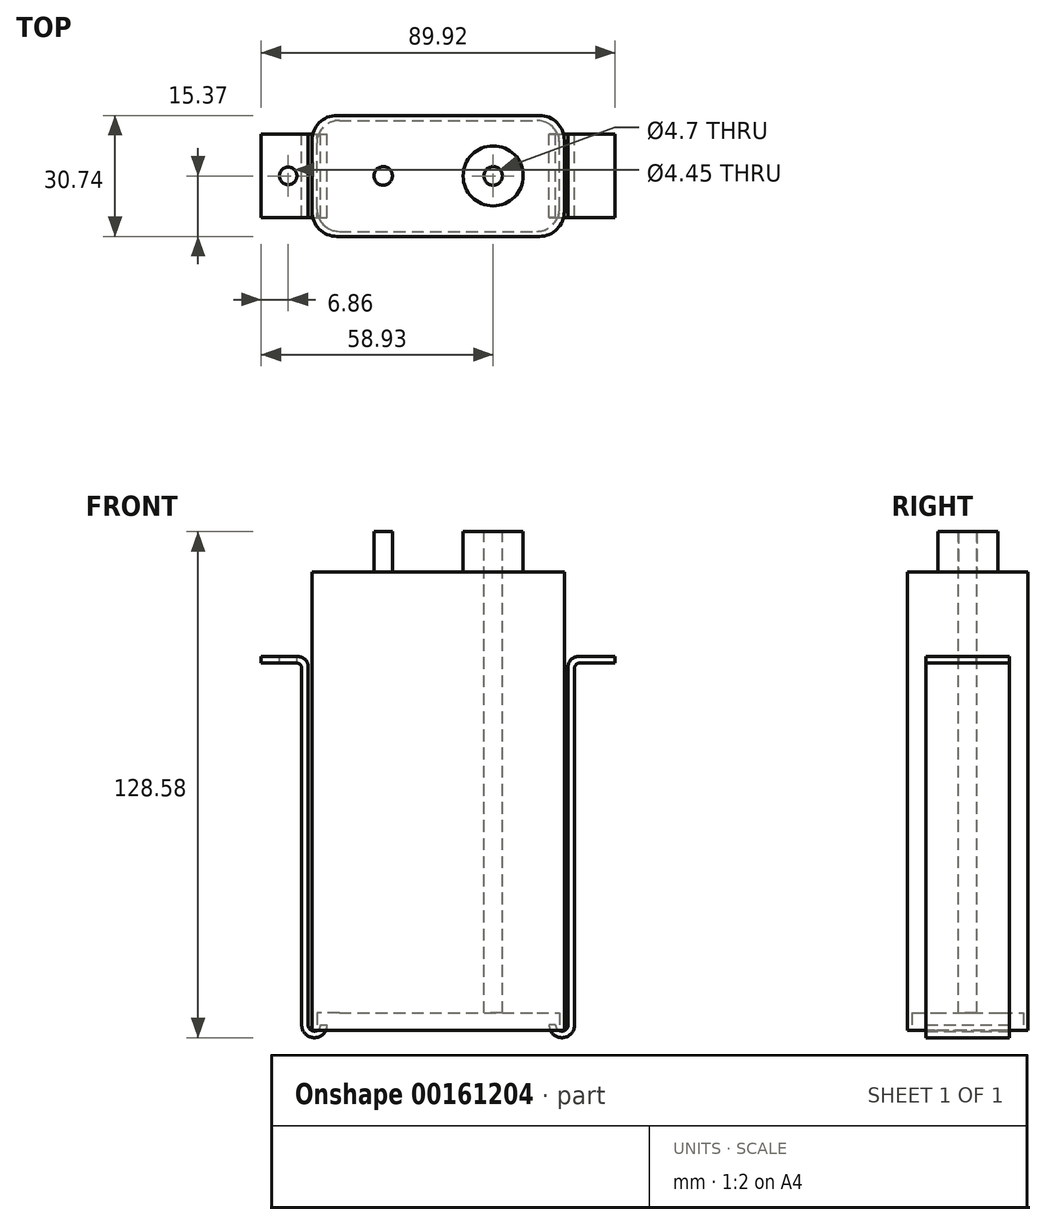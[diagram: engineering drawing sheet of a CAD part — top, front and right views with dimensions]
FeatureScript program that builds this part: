
annotation { "Feature Type Name" : "Feature", "Feature Type Description" : "" }
export const myFeature = defineFeature(function(context is Context, id is Id, definition is map)
    precondition{}
    {
        {
            var Q0;
            Q0=qCreatedBy(makeId("Top.planeOp"),FACE);
            var sketch = newSketch(context, id + "F0", { "sketchPlane" : qUnion([Q0])});
            skLineSegment(sketch, "E0.bottom", {"start": v(25.72, 15.37) * mm, "end": v(-25.72, 15.37) * mm});
            skLineSegment(sketch, "E0.top", {"start": v(25.72, -15.37) * mm, "end": v(-25.72, -15.37) * mm});
            skLineSegment(sketch, "E0.left", {"start": v(32.07, 9.02) * mm, "end": v(32.07, -9.02) * mm});
            skLineSegment(sketch, "E0.right", {"start": v(-32.07, 9.02) * mm, "end": v(-32.07, -9.02) * mm});
            skPoint(sketch, "E0.middle", {"position": v(0, 0) * mm});
            skPoint(sketch, "E1.visualSharp", {"position": v(-32.07, 15.37) * mm});
            skArc(sketch, "E1.filletArc", {"start": v(-25.72, 15.37) * mm, "mid": v(-30.2, 13.5) * mm, "end": v(-32.07, 9.02) * mm});
            skPoint(sketch, "E2.visualSharp", {"position": v(-32.07, -15.37) * mm});
            skArc(sketch, "E2.filletArc", {"start": v(-32.07, -9.02) * mm, "mid": v(-30.2, -13.5) * mm, "end": v(-25.72, -15.37) * mm});
            skPoint(sketch, "E3.visualSharp", {"position": v(32.07, -15.37) * mm});
            skArc(sketch, "E3.filletArc", {"start": v(25.72, -15.37) * mm, "mid": v(30.2, -13.5) * mm, "end": v(32.07, -9.02) * mm});
            skPoint(sketch, "E4.visualSharp", {"position": v(32.07, 15.37) * mm});
            skArc(sketch, "E4.filletArc", {"start": v(32.07, 9.02) * mm, "mid": v(30.2, 13.5) * mm, "end": v(25.72, 15.37) * mm});
            skCircle(sketch, "E5", {"center": v(-13.97, 0) * mm, "radius": 7.62 * mm});
            skCircle(sketch, "E6.MirrorC", {"center": v(13.97, 0) * mm, "radius": 7.62 * mm});
            skCircle(sketch, "E7", {"center": v(-13.97, 0) * mm, "radius": 2.35 * mm});
            skCircle(sketch, "E8.MirrorC", {"center": v(13.97, 0) * mm, "radius": 2.35 * mm});
            skSolve(sketch);
        }
        {
            var Q0;
            Q0=makeQuery(id+"F0.imprint","IMPRINT",FACE,{"disambiguationData":[TD([[makeQuery(id+"F0.imprint","IMPRINT",EDGE,{"derivedFrom":sQuery(id+"F0.wireOp",EDGE,"E0.bottom")}),1.0]])]});
            var Q1;
            Q1=makeQuery(id+"F0.imprint","IMPRINT",FACE,{"disambiguationData":[TD([[makeQuery(id+"F0.imprint","IMPRINT",EDGE,{"derivedFrom":sQuery(id+"F0.wireOp",EDGE,"E5")}),1.0]])]});
            var Q2;
            Q2=makeQuery(id+"F0.imprint","IMPRINT",FACE,{"disambiguationData":[TD([[makeQuery(id+"F0.imprint","IMPRINT",EDGE,{"derivedFrom":sQuery(id+"F0.wireOp",EDGE,"E7")}),1.0]])]});
            var Q3;
            Q3=makeQuery(id+"F0.imprint","IMPRINT",FACE,{"disambiguationData":[TD([[makeQuery(id+"F0.imprint","IMPRINT",EDGE,{"derivedFrom":sQuery(id+"F0.wireOp",EDGE,"E6.MirrorC")}),-1.0]])]});
            var Q4;
            Q4=makeQuery(id+"F0.imprint","IMPRINT",FACE,{"disambiguationData":[TD([[makeQuery(id+"F0.imprint","IMPRINT",EDGE,{"derivedFrom":sQuery(id+"F0.wireOp",EDGE,"E8.MirrorC")}),-1.0]])]});
            extrude(context, id + "F1", {"entities" : qUnion([Q0, Q1, Q2, Q3, Q4]), "oppositeDirection" : true, "depth" : 98.17 * mm});
        }
        {
            var Q0;
            Q0=makeQuery(id+"F0.imprint","IMPRINT",FACE,{"disambiguationData":[TD([[makeQuery(id+"F0.imprint","IMPRINT",EDGE,{"derivedFrom":sQuery(id+"F0.wireOp",EDGE,"E5")}),1.0]])]});
            var Q1;
            Q1=makeQuery(id+"F0.imprint","IMPRINT",FACE,{"disambiguationData":[TD([[makeQuery(id+"F0.imprint","IMPRINT",EDGE,{"derivedFrom":sQuery(id+"F0.wireOp",EDGE,"E7")}),1.0]])]});
            var Q2;
            Q2=makeQuery(id+"F0.imprint","IMPRINT",FACE,{"disambiguationData":[TD([[makeQuery(id+"F0.imprint","IMPRINT",EDGE,{"derivedFrom":sQuery(id+"F0.wireOp",EDGE,"E6.MirrorC")}),-1.0]])]});
            var Q3;
            Q3=makeQuery(id+"F0.imprint","IMPRINT",FACE,{"disambiguationData":[TD([[makeQuery(id+"F0.imprint","IMPRINT",EDGE,{"derivedFrom":sQuery(id+"F0.wireOp",EDGE,"E8.MirrorC")}),-1.0]])]});
            extrude(context, id + "F2", {"entities" : qUnion([Q0, Q1, Q2, Q3]), "operationType" : NewBodyOperationType.ADD, "depth" : 18.29 * mm});
        }
        {
            var Q0;
            Q0=makeQuery(id+"F0.imprint","IMPRINT",FACE,{"disambiguationData":[TD([[makeQuery(id+"F0.imprint","IMPRINT",EDGE,{"derivedFrom":sQuery(id+"F0.wireOp",EDGE,"E7")}),1.0]])]});
            var Q1;
            Q1=makeQuery(id+"F0.imprint","IMPRINT",FACE,{"disambiguationData":[TD([[makeQuery(id+"F0.imprint","IMPRINT",EDGE,{"derivedFrom":sQuery(id+"F0.wireOp",EDGE,"E8.MirrorC")}),-1.0]])]});
            extrude(context, id + "F3", {"entities" : qUnion([Q0, Q1]), "operationType" : NewBodyOperationType.ADD, "depth" : 28.57 * mm});
        }
        {
            var Q0;
            Q0=makeQuery(id+"F1.opExtrude","CAP_FACE",FACE,{"disambiguationData":[OSD([sQuery(id+"F0.wireOp",EDGE,"E0.bottom"),sQuery(id+"F0.wireOp",EDGE,"E0.top"),sQuery(id+"F0.wireOp",EDGE,"E0.left"),sQuery(id+"F0.wireOp",EDGE,"E0.right"),sQuery(id+"F0.wireOp",EDGE,"E1.filletArc"),sQuery(id+"F0.wireOp",EDGE,"E2.filletArc"),sQuery(id+"F0.wireOp",EDGE,"E3.filletArc"),sQuery(id+"F0.wireOp",EDGE,"E4.filletArc")])],"isStart":false});
            var sketch = newSketch(context, id + "F4", { "sketchPlane" : qUnion([Q0])});
            skLineSegment(sketch, "E9", {"start": v(-25.08, 14.1) * mm, "end": v(25.08, 14.1) * mm});
            skLineSegment(sketch, "E10", {"start": v(30.8, 8.38) * mm, "end": v(30.8, -8.38) * mm});
            skLineSegment(sketch, "E11.MirrorCS", {"start": v(-25.08, -14.1) * mm, "end": v(25.08, -14.1) * mm});
            skLineSegment(sketch, "E12.MirrorCS", {"start": v(-30.8, 8.38) * mm, "end": v(-30.8, -8.38) * mm});
            skPoint(sketch, "E13.orphan", {"position": v(-12.64, 14.1) * mm});
            skPoint(sketch, "E14.orphan", {"position": v(-30.8, 5.97) * mm});
            skPoint(sketch, "E15.orphan", {"position": v(-30.8, -3.63) * mm});
            skPoint(sketch, "E16.orphan", {"position": v(-12.64, -14.1) * mm});
            skPoint(sketch, "E17.orphan", {"position": v(14.72, -14.1) * mm});
            skPoint(sketch, "E18.orphan", {"position": v(30.8, -3.63) * mm});
            skPoint(sketch, "E19.orphan", {"position": v(30.8, 5.97) * mm});
            skPoint(sketch, "E20.orphan", {"position": v(14.72, 14.1) * mm});
            skPoint(sketch, "E21.visualSharp", {"position": v(-30.8, 14.1) * mm});
            skArc(sketch, "E21.filletArc", {"start": v(-25.08, 14.1) * mm, "mid": v(-29.12, 12.42) * mm, "end": v(-30.8, 8.38) * mm});
            skPoint(sketch, "E22.visualSharp", {"position": v(-30.8, -14.1) * mm});
            skArc(sketch, "E22.filletArc", {"start": v(-30.8, -8.38) * mm, "mid": v(-29.12, -12.42) * mm, "end": v(-25.08, -14.1) * mm});
            skPoint(sketch, "E23.visualSharp", {"position": v(30.8, 14.1) * mm});
            skArc(sketch, "E23.filletArc", {"start": v(30.8, 8.38) * mm, "mid": v(29.12, 12.42) * mm, "end": v(25.08, 14.1) * mm});
            skPoint(sketch, "E24.visualSharp", {"position": v(30.8, -14.1) * mm});
            skArc(sketch, "E24.filletArc", {"start": v(25.08, -14.1) * mm, "mid": v(29.12, -12.42) * mm, "end": v(30.8, -8.38) * mm});
            skSolve(sketch);
        }
        {
            var Q0;
            Q0=makeQuery(id+"F4.imprint","IMPRINT",FACE,{"disambiguationData":[TD([[makeQuery(id+"F4.imprint","IMPRINT",EDGE,{"derivedFrom":sQuery(id+"F4.wireOp",EDGE,"E9")}),-1.0]])]});
            extrude(context, id + "F5", {"entities" : qUnion([Q0]), "operationType" : NewBodyOperationType.REMOVE, "oppositeDirection" : true, "depth" : 4.44 * mm});
        }
        {
            var Q0;
            Q0=qCreatedBy(makeId("Front.planeOp"),FACE);
            var sketch = newSketch(context, id + "F6", { "sketchPlane" : qUnion([Q0])});
            skLineSegment(sketch, "E25", {"start": v(-31.43, 47.26) * mm, "end": v(-31.43, -154.86) * mm, "construction": true});
            skArc(sketch, "E26", {"start": v(-33.02, -96.76) * mm, "mid": v(-31.43, -98.35) * mm, "end": v(-29.84, -96.76) * mm});
            skArc(sketch, "E27", {"start": v(-34.67, -96.76) * mm, "mid": v(-31.43, -100) * mm, "end": v(-28.2, -96.76) * mm});
            skLineSegment(sketch, "E28", {"start": v(-29.84, -96.76) * mm, "end": v(-28.2, -96.76) * mm});
            skLineSegment(sketch, "E29", {"start": v(-33.02, -96.76) * mm, "end": v(-33.02, -5.71) * mm});
            skLineSegment(sketch, "E30", {"start": v(-34.67, -96.76) * mm, "end": v(-34.67, -6.1) * mm});
            skLineSegment(sketch, "E31", {"start": v(-35.56, -3.18) * mm, "end": v(-44.96, -3.18) * mm});
            skLineSegment(sketch, "E32", {"start": v(-44.96, -4.83) * mm, "end": v(-35.94, -4.83) * mm});
            skLineSegment(sketch, "E33", {"start": v(-44.96, -3.18) * mm, "end": v(-44.96, -4.83) * mm});
            skPoint(sketch, "E34.orphan", {"position": v(-44.96, -2.41) * mm});
            skPoint(sketch, "E35.orphan", {"position": v(-35.42, -4.83) * mm});
            skPoint(sketch, "E36.orphan", {"position": v(-33.02, -2.22) * mm});
            skPoint(sketch, "E37.orphan", {"position": v(-32.78, -3.18) * mm});
            skPoint(sketch, "E38.visualSharp", {"position": v(-33.02, -3.18) * mm});
            skArc(sketch, "E38.filletArc", {"start": v(-33.02, -5.71) * mm, "mid": v(-33.76, -3.92) * mm, "end": v(-35.56, -3.17) * mm});
            skPoint(sketch, "E39.visualSharp", {"position": v(-34.67, -4.83) * mm});
            skArc(sketch, "E39.filletArc", {"start": v(-34.67, -6.1) * mm, "mid": v(-35.04, -5.2) * mm, "end": v(-35.94, -4.83) * mm});
            skLineSegment(sketch, "E40.MirrorCS", {"start": v(29.84, -96.76) * mm, "end": v(28.2, -96.76) * mm});
            skArc(sketch, "E41.MirrorCS", {"start": v(34.67, -96.76) * mm, "mid": v(31.43, -100) * mm, "end": v(28.2, -96.76) * mm});
            skArc(sketch, "E42.MirrorCS", {"start": v(33.02, -96.76) * mm, "mid": v(31.43, -98.35) * mm, "end": v(29.84, -96.76) * mm});
            skLineSegment(sketch, "E43.MirrorCS", {"start": v(33.02, -96.76) * mm, "end": v(33.02, -5.71) * mm});
            skLineSegment(sketch, "E44.MirrorCS", {"start": v(34.67, -96.76) * mm, "end": v(34.67, -6.1) * mm});
            skArc(sketch, "E45.MirrorCS", {"start": v(34.67, -6.1) * mm, "mid": v(35.04, -5.2) * mm, "end": v(35.94, -4.83) * mm});
            skArc(sketch, "E46.MirrorCS", {"start": v(33.02, -5.71) * mm, "mid": v(33.76, -3.92) * mm, "end": v(35.56, -3.17) * mm});
            skLineSegment(sketch, "E47.MirrorCS", {"start": v(44.96, -4.83) * mm, "end": v(35.94, -4.83) * mm});
            skLineSegment(sketch, "E48.MirrorCS", {"start": v(35.56, -3.18) * mm, "end": v(44.96, -3.18) * mm});
            skLineSegment(sketch, "E49.MirrorCS", {"start": v(44.96, -3.18) * mm, "end": v(44.96, -4.83) * mm});
            skSolve(sketch);
        }
        {
            var Q0;
            Q0=makeQuery(id+"F6.imprint","IMPRINT",FACE,{"disambiguationData":[TD([[makeQuery(id+"F6.imprint","IMPRINT",EDGE,{"derivedFrom":sQuery(id+"F6.wireOp",EDGE,"E26")}),-1.0]])]});
            var Q1;
            Q1=makeQuery(id+"F6.imprint","IMPRINT",FACE,{"disambiguationData":[TD([[makeQuery(id+"F6.imprint","IMPRINT",EDGE,{"derivedFrom":sQuery(id+"F6.wireOp",EDGE,"E40.MirrorCS")}),1.0]])]});
            extrude(context, id + "F7", {"entities" : qUnion([Q0, Q1]), "operationType" : NewBodyOperationType.ADD, "endBound" : BoundingType.SYMMETRIC, "depth" : 21.2 * mm});
        }
        {
            var Q0;
            Q0=makeQuery(id+"F7.opExtrude","SWEPT_FACE",FACE,{"disambiguationData":[OSD([sQuery(id+"F6.wireOp",EDGE,"E31")])]});
            var sketch = newSketch(context, id + "F8", { "sketchPlane" : qUnion([Q0])});
            skCircle(sketch, "E50", {"center": v(-38.1, 0) * mm, "radius": 2.22 * mm});
            skCircle(sketch, "E51.MirrorC", {"center": v(38.1, 0) * mm, "radius": 2.22 * mm});
            skSolve(sketch);
        }
        {
            var Q0;
            Q0=makeQuery(id+"F8.imprint","IMPRINT",FACE,{"disambiguationData":[TD([[makeQuery(id+"F8.imprint","IMPRINT",EDGE,{"derivedFrom":sQuery(id+"F8.wireOp",EDGE,"E51.MirrorC")}),-1.0]])]});
            var Q1;
            Q1=makeQuery(id+"F8.imprint","IMPRINT",FACE,{"disambiguationData":[TD([[makeQuery(id+"F8.imprint","IMPRINT",EDGE,{"derivedFrom":sQuery(id+"F8.wireOp",EDGE,"E50")}),1.0]])]});
            extrude(context, id + "F9", {"entities" : qUnion([Q0, Q1]), "operationType" : NewBodyOperationType.REMOVE, "oppositeDirection" : true, "depth" : 2.54 * mm});
        }
    });
